# Revit family: result
name_source: partatom
category: Plumbing Fixtures
revit_build: Autodesk Revit 2015 (Build: 20140903_1530(x64)
units: mm (PartAtom-declared; Revit-internal decimal feet)

## types (1)
- Default
    BIMobject category = Taps & Mixers
    BIMobject category code = sanitary-taps-mixers
    BIMobject main category = Sanitary
    BIMobject main category code = sanitary
    Brand url = http://www.duravit.com
    Design country = Germany
    Edition number = 1
    IFC Classification = Valve
    Installation instructions = http://pro.duravit.com
    Manufacturer name = DURAVIT AG
    Masterformat 2014 Code = 22 41 39
    Masterformat 2014 Description = Residential Faucets, Supplies, and Trim
    Material main = Chrome
    OmniClass Code = 23-31 11 00
    OmniClass Description = Faucets
    Product Guid = 0b10469b-5c11-47be-976e-31b261346d9f
    Product SKU = A1-Single-lever-washbasin-mixer-137x43x125-mm-A11010
    Product certification = http://pro.duravit.com
    Product data url = https://bimobject.com
    Product family = A.1
    Product group = Tap and mixer
    Product name = A.1 Single lever washbasin mixer 137x43x125 mm - A11010
    Product url = http://pro.duravit.com
    QR code = http://bimobject.com
    Technical description = http://pro.duravit.com
    UNSPSC Code = 301815
    Uniclass 2015 Code = Pr_40_20_87_98
    Uniclass 2015 Name = Washbasin taps
    Uniformat II Code = D2010
    Uniformat II Description = Plumbing Fixtures
    Youtube clip = http://pro.duravit.com

## geometry (parser evidence)
native form markers: Sweep x4
no freeform markers — native parametric forms only
